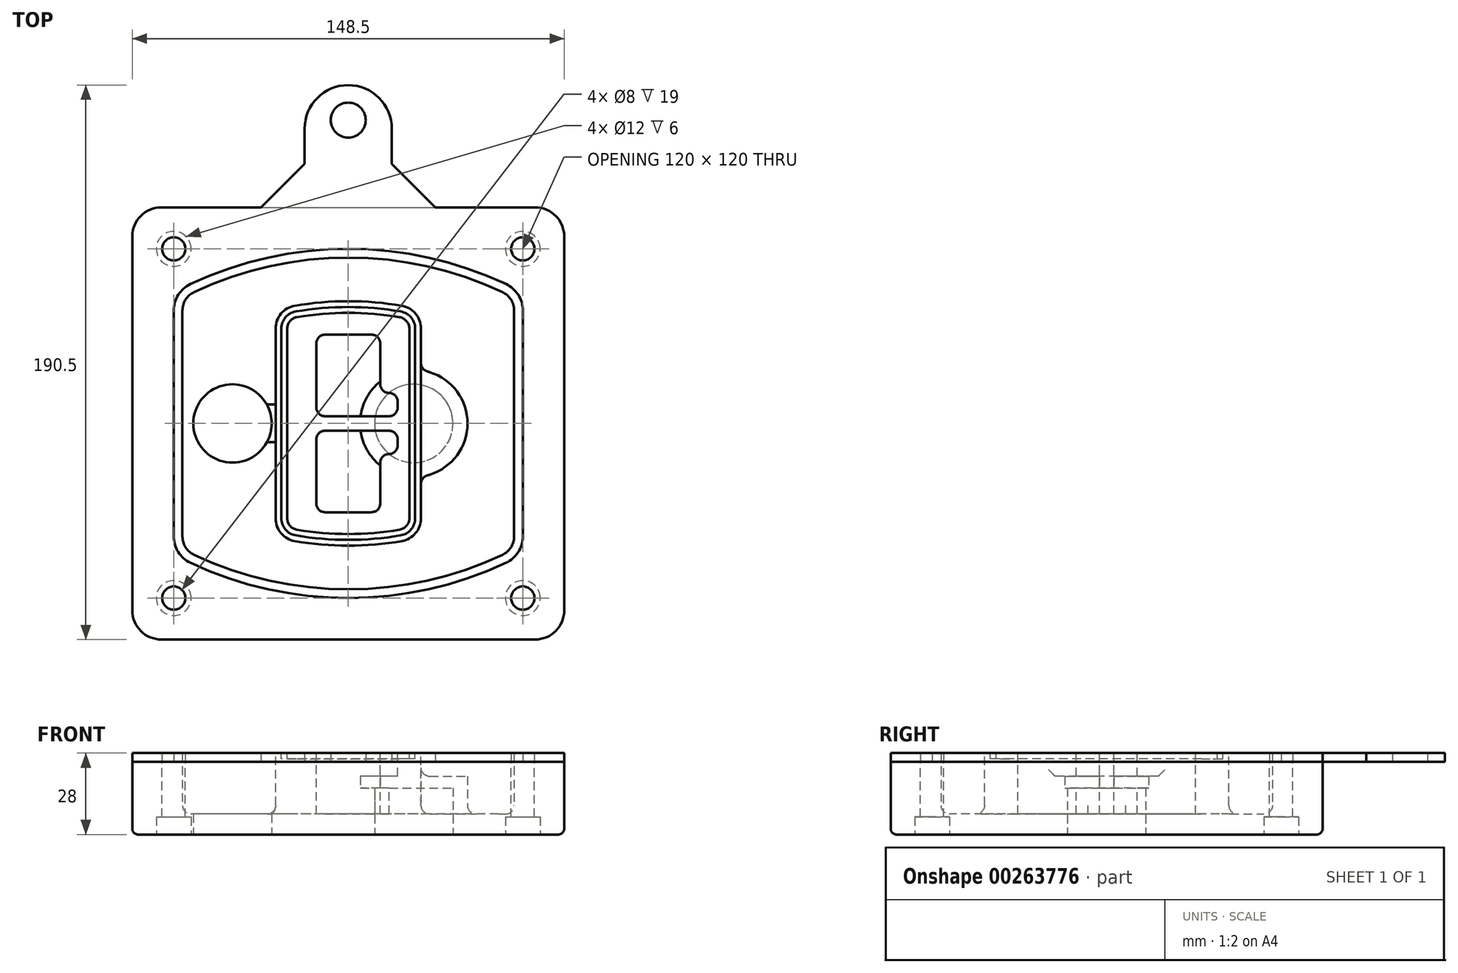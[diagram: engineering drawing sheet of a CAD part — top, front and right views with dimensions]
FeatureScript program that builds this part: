
annotation { "Feature Type Name" : "Feature", "Feature Type Description" : "" }
export const myFeature = defineFeature(function(context is Context, id is Id, definition is map)
    precondition{}
    {
        {
            var Q0;
            Q0=qCreatedBy(makeId("Top.planeOp"),FACE);
            var sketch = newSketch(context, id + "F0", { "sketchPlane" : qUnion([Q0])});
            skPoint(sketch, "E0.rect.middle", {"position": v(0, 0) * mm});
            skLineSegment(sketch, "E1.bottom", {"start": v(-64.25, -74.25) * mm, "end": v(64.25, -74.25) * mm});
            skLineSegment(sketch, "E1.top", {"start": v(-64.25, 74.25) * mm, "end": v(64.25, 74.25) * mm});
            skLineSegment(sketch, "E1.left", {"start": v(-74.25, -64.25) * mm, "end": v(-74.25, 64.25) * mm});
            skLineSegment(sketch, "E1.right", {"start": v(74.25, -64.25) * mm, "end": v(74.25, 64.25) * mm});
            skLineSegment(sketch, "E2", {"start": v(-74.25, 74.25) * mm, "end": v(74.25, -74.25) * mm, "construction": true});
            skLineSegment(sketch, "E3", {"start": v(74.25, 74.25) * mm, "end": v(-74.25, -74.25) * mm, "construction": true});
            skCircle(sketch, "E4", {"center": v(-60, 60) * mm, "radius": 4 * mm});
            skCircle(sketch, "E5", {"center": v(60, 60) * mm, "radius": 4 * mm});
            skCircle(sketch, "E6", {"center": v(60, -60) * mm, "radius": 4 * mm});
            skCircle(sketch, "E7", {"center": v(-60, -60) * mm, "radius": 4 * mm});
            skLineSegment(sketch, "E8", {"start": v(-60, 60) * mm, "end": v(60, 60) * mm, "construction": true});
            skLineSegment(sketch, "E9", {"start": v(60, 60) * mm, "end": v(60, -60) * mm, "construction": true});
            skLineSegment(sketch, "E10", {"start": v(60, -60) * mm, "end": v(-60, -60) * mm, "construction": true});
            skLineSegment(sketch, "E11", {"start": v(-60, -60) * mm, "end": v(-60, 60) * mm, "construction": true});
            skLineSegment(sketch, "E12", {"start": v(-60, 38.83) * mm, "end": v(-60, -38.83) * mm});
            skLineSegment(sketch, "E13", {"start": v(60, 38.83) * mm, "end": v(60, -38.83) * mm});
            skArc(sketch, "E14", {"start": v(54.26, 47.88) * mm, "mid": v(0, 60) * mm, "end": v(-54.26, 47.88) * mm});
            skArc(sketch, "E15", {"start": v(-54.26, -47.88) * mm, "mid": v(0, -60) * mm, "end": v(54.26, -47.88) * mm});
            skLineSegment(sketch, "E16", {"start": v(-60, 0) * mm, "end": v(60, 0) * mm, "construction": true});
            skPoint(sketch, "E17.visualSharp", {"position": v(-60, -45) * mm});
            skArc(sketch, "E17.filletArc", {"start": v(-60, -38.83) * mm, "mid": v(-58.44, -44.2) * mm, "end": v(-54.26, -47.88) * mm});
            skPoint(sketch, "E18.visualSharp", {"position": v(-60, 45) * mm});
            skArc(sketch, "E18.filletArc", {"start": v(-54.26, 47.88) * mm, "mid": v(-58.44, 44.2) * mm, "end": v(-60, 38.83) * mm});
            skPoint(sketch, "E19.visualSharp", {"position": v(60, 45) * mm});
            skArc(sketch, "E19.filletArc", {"start": v(60, 38.83) * mm, "mid": v(58.44, 44.2) * mm, "end": v(54.26, 47.88) * mm});
            skPoint(sketch, "E20.visualSharp", {"position": v(60, -45) * mm});
            skArc(sketch, "E20.filletArc", {"start": v(54.26, -47.88) * mm, "mid": v(58.44, -44.2) * mm, "end": v(60, -38.83) * mm});
            skPoint(sketch, "E21.visualSharp", {"position": v(-74.25, 74.25) * mm});
            skArc(sketch, "E21.filletArc", {"start": v(-64.25, 74.25) * mm, "mid": v(-71.32, 71.32) * mm, "end": v(-74.25, 64.25) * mm});
            skPoint(sketch, "E22.visualSharp", {"position": v(74.25, 74.25) * mm});
            skArc(sketch, "E22.filletArc", {"start": v(74.25, 64.25) * mm, "mid": v(71.32, 71.32) * mm, "end": v(64.25, 74.25) * mm});
            skPoint(sketch, "E23.visualSharp", {"position": v(74.25, -74.25) * mm});
            skArc(sketch, "E23.filletArc", {"start": v(64.25, -74.25) * mm, "mid": v(71.32, -71.32) * mm, "end": v(74.25, -64.25) * mm});
            skPoint(sketch, "E24.visualSharp", {"position": v(-74.25, -74.25) * mm});
            skArc(sketch, "E24.filletArc", {"start": v(-74.25, -64.25) * mm, "mid": v(-71.32, -71.32) * mm, "end": v(-64.25, -74.25) * mm});
            skArc(sketch, "E25.0", {"start": v(57, 38.83) * mm, "mid": v(55.9, 42.58) * mm, "end": v(52.98, 45.17) * mm});
            skLineSegment(sketch, "E25.1", {"start": v(57, 38.83) * mm, "end": v(57, -38.83) * mm});
            skArc(sketch, "E25.2", {"start": v(52.98, -45.17) * mm, "mid": v(55.9, -42.58) * mm, "end": v(57, -38.83) * mm});
            skArc(sketch, "E25.3", {"start": v(-52.98, -45.17) * mm, "mid": v(0, -57) * mm, "end": v(52.98, -45.17) * mm});
            skArc(sketch, "E25.4", {"start": v(-57, -38.83) * mm, "mid": v(-55.9, -42.58) * mm, "end": v(-52.98, -45.17) * mm});
            skArc(sketch, "E25.5", {"start": v(52.98, 45.17) * mm, "mid": v(0, 57) * mm, "end": v(-52.98, 45.17) * mm});
            skLineSegment(sketch, "E25.6", {"start": v(-57, 38.83) * mm, "end": v(-57, -38.83) * mm});
            skArc(sketch, "E25.7", {"start": v(-52.98, 45.17) * mm, "mid": v(-55.9, 42.58) * mm, "end": v(-57, 38.83) * mm});
            skArc(sketch, "E26.0", {"start": v(-55.96, 51.5) * mm, "mid": v(-61.82, 46.33) * mm, "end": v(-64, 38.83) * mm});
            skArc(sketch, "E26.1", {"start": v(55.96, 51.5) * mm, "mid": v(0, 64) * mm, "end": v(-55.96, 51.5) * mm});
            skArc(sketch, "E26.2", {"start": v(64, 38.83) * mm, "mid": v(61.82, 46.33) * mm, "end": v(55.96, 51.5) * mm});
            skLineSegment(sketch, "E26.3", {"start": v(64, 38.83) * mm, "end": v(64, -38.83) * mm});
            skArc(sketch, "E26.4", {"start": v(55.96, -51.5) * mm, "mid": v(61.82, -46.33) * mm, "end": v(64, -38.83) * mm});
            skLineSegment(sketch, "E26.5", {"start": v(-64, 38.83) * mm, "end": v(-64, -38.83) * mm});
            skArc(sketch, "E26.6", {"start": v(-55.96, -51.5) * mm, "mid": v(0, -64) * mm, "end": v(55.96, -51.5) * mm});
            skArc(sketch, "E26.7", {"start": v(-64, -38.83) * mm, "mid": v(-61.82, -46.33) * mm, "end": v(-55.96, -51.5) * mm});
            skSolve(sketch);
        }
        {
            var Q0;
            Q0=makeQuery(id+"F0.imprint","IMPRINT",FACE,{"disambiguationData":[TD([[makeQuery(id+"F0.imprint","IMPRINT",EDGE,{"derivedFrom":sQuery(id+"F0.wireOp",EDGE,"E1.bottom")}),1.0]])]});
            var Q1;
            Q1=makeQuery(id+"F0.imprint","IMPRINT",FACE,{"disambiguationData":[TD([[makeQuery(id+"F0.imprint","IMPRINT",EDGE,{"derivedFrom":sQuery(id+"F0.wireOp",EDGE,"E12")}),1.0]])]});
            var Q2;
            Q2=makeQuery(id+"F0.imprint","IMPRINT",FACE,{"disambiguationData":[TD([[makeQuery(id+"F0.imprint","IMPRINT",EDGE,{"derivedFrom":sQuery(id+"F0.wireOp",EDGE,"E25.0")}),1.0]])]});
            var Q3;
            Q3=makeQuery(id+"F0.imprint","IMPRINT",FACE,{"disambiguationData":[TD([[makeQuery(id+"F0.imprint","IMPRINT",EDGE,{"derivedFrom":sQuery(id+"F0.wireOp",EDGE,"E12")}),-1.0]])]});
            extrude(context, id + "F1", {"entities" : qUnion([Q0, Q1, Q2, Q3]), "oppositeDirection" : true, "depth" : 25 * mm});
        }
        {
            var Q0;
            Q0=makeQuery(id+"F0.imprint","IMPRINT",FACE,{"disambiguationData":[TD([[makeQuery(id+"F0.imprint","IMPRINT",EDGE,{"derivedFrom":sQuery(id+"F0.wireOp",EDGE,"E12")}),1.0]])]});
            extrude(context, id + "F2", {"entities" : qUnion([Q0]), "operationType" : NewBodyOperationType.ADD, "depth" : 3 * mm});
        }
        {
            var Q0;
            Q0=makeQuery(id+"F0.imprint","IMPRINT",FACE,{"disambiguationData":[TD([[makeQuery(id+"F0.imprint","IMPRINT",EDGE,{"derivedFrom":sQuery(id+"F0.wireOp",EDGE,"E25.0")}),1.0]])]});
            extrude(context, id + "F3", {"entities" : qUnion([Q0]), "operationType" : NewBodyOperationType.REMOVE, "oppositeDirection" : true, "depth" : 18 * mm});
        }
        {
            var Q0;
            Q0=makeQuery(id+"F2.opExtrude","CAP_FACE",FACE,{"disambiguationData":[OSD([sQuery(id+"F0.wireOp",EDGE,"E12"),sQuery(id+"F0.wireOp",EDGE,"E13"),sQuery(id+"F0.wireOp",EDGE,"E14"),sQuery(id+"F0.wireOp",EDGE,"E15"),sQuery(id+"F0.wireOp",EDGE,"E17.filletArc"),sQuery(id+"F0.wireOp",EDGE,"E18.filletArc"),sQuery(id+"F0.wireOp",EDGE,"E19.filletArc"),sQuery(id+"F0.wireOp",EDGE,"E20.filletArc"),sQuery(id+"F0.wireOp",EDGE,"E25.0"),sQuery(id+"F0.wireOp",EDGE,"E25.1"),sQuery(id+"F0.wireOp",EDGE,"E25.2"),sQuery(id+"F0.wireOp",EDGE,"E25.3"),sQuery(id+"F0.wireOp",EDGE,"E25.4"),sQuery(id+"F0.wireOp",EDGE,"E25.5"),sQuery(id+"F0.wireOp",EDGE,"E25.6"),sQuery(id+"F0.wireOp",EDGE,"E25.7")])],"isStart":false});
            var sketch = newSketch(context, id + "F4", { "sketchPlane" : qUnion([Q0])});
            skArc(sketch, "E27.0", {"start": v(-18.34, -40.45) * mm, "mid": v(0, -42) * mm, "end": v(18.34, -40.45) * mm});
            skArc(sketch, "E28.0", {"start": v(18.34, 40.45) * mm, "mid": v(0, 42) * mm, "end": v(-18.34, 40.45) * mm});
            skLineSegment(sketch, "E29", {"start": v(-25, 32.57) * mm, "end": v(-25, -32.57) * mm});
            skLineSegment(sketch, "E30", {"start": v(25, 32.57) * mm, "end": v(25, -32.57) * mm});
            skLineSegment(sketch, "E31", {"start": v(-25, 39.1) * mm, "end": v(25, 39.1) * mm, "construction": true});
            skLineSegment(sketch, "E32", {"start": v(-25, -39.1) * mm, "end": v(25, -39.1) * mm, "construction": true});
            skPoint(sketch, "E33.visualSharp", {"position": v(-25, 39.1) * mm});
            skArc(sketch, "E33.filletArc", {"start": v(-18.34, 40.45) * mm, "mid": v(-23.11, 37.73) * mm, "end": v(-25, 32.57) * mm});
            skPoint(sketch, "E34.visualSharp", {"position": v(25, 39.1) * mm});
            skArc(sketch, "E34.filletArc", {"start": v(25, 32.57) * mm, "mid": v(23.11, 37.73) * mm, "end": v(18.34, 40.45) * mm});
            skPoint(sketch, "E35.visualSharp", {"position": v(25, -39.1) * mm});
            skArc(sketch, "E35.filletArc", {"start": v(18.34, -40.45) * mm, "mid": v(23.11, -37.73) * mm, "end": v(25, -32.57) * mm});
            skPoint(sketch, "E36.visualSharp", {"position": v(-25, -39.1) * mm});
            skArc(sketch, "E36.filletArc", {"start": v(-25, -32.57) * mm, "mid": v(-23.11, -37.73) * mm, "end": v(-18.34, -40.45) * mm});
            skArc(sketch, "E37.0", {"start": v(52.98, 45.17) * mm, "mid": v(0, 57) * mm, "end": v(-52.98, 45.17) * mm});
            skArc(sketch, "E37.1", {"start": v(-52.98, 45.17) * mm, "mid": v(-55.9, 42.58) * mm, "end": v(-57, 38.83) * mm});
            skLineSegment(sketch, "E37.2", {"start": v(-57, 38.83) * mm, "end": v(-57, -38.83) * mm});
            skArc(sketch, "E37.3", {"start": v(-57, -38.83) * mm, "mid": v(-55.9, -42.58) * mm, "end": v(-52.98, -45.17) * mm});
            skArc(sketch, "E37.4", {"start": v(-52.98, -45.17) * mm, "mid": v(0, -57) * mm, "end": v(52.98, -45.17) * mm});
            skArc(sketch, "E37.5", {"start": v(52.98, -45.17) * mm, "mid": v(55.9, -42.58) * mm, "end": v(57, -38.83) * mm});
            skLineSegment(sketch, "E37.6", {"start": v(57, 38.83) * mm, "end": v(57, -38.83) * mm});
            skArc(sketch, "E37.7", {"start": v(57, 38.83) * mm, "mid": v(55.9, 42.58) * mm, "end": v(52.98, 45.17) * mm});
            skLineSegment(sketch, "E38.0", {"start": v(23, 32.57) * mm, "end": v(23, -32.57) * mm});
            skArc(sketch, "E38.1", {"start": v(18, -38.48) * mm, "mid": v(21.58, -36.44) * mm, "end": v(23, -32.57) * mm});
            skArc(sketch, "E38.2", {"start": v(-18, -38.48) * mm, "mid": v(0, -40) * mm, "end": v(18, -38.48) * mm});
            skArc(sketch, "E38.3", {"start": v(-23, -32.57) * mm, "mid": v(-21.58, -36.44) * mm, "end": v(-18, -38.48) * mm});
            skLineSegment(sketch, "E38.4", {"start": v(-23, 32.57) * mm, "end": v(-23, -32.57) * mm});
            skArc(sketch, "E38.5", {"start": v(23, 32.57) * mm, "mid": v(21.58, 36.44) * mm, "end": v(18, 38.48) * mm});
            skArc(sketch, "E38.6", {"start": v(-18, 38.48) * mm, "mid": v(-21.58, 36.44) * mm, "end": v(-23, 32.57) * mm});
            skArc(sketch, "E38.7", {"start": v(18, 38.48) * mm, "mid": v(0, 40) * mm, "end": v(-18, 38.48) * mm});
            skArc(sketch, "E39.0", {"start": v(21, 32.57) * mm, "mid": v(20.06, 35.15) * mm, "end": v(17.67, 36.5) * mm});
            skLineSegment(sketch, "E39.1", {"start": v(21, 32.57) * mm, "end": v(21, -32.57) * mm});
            skArc(sketch, "E39.2", {"start": v(17.67, -36.5) * mm, "mid": v(20.06, -35.15) * mm, "end": v(21, -32.57) * mm});
            skArc(sketch, "E39.3", {"start": v(-17.67, -36.5) * mm, "mid": v(0, -38) * mm, "end": v(17.67, -36.5) * mm});
            skArc(sketch, "E39.4", {"start": v(-21, -32.57) * mm, "mid": v(-20.06, -35.15) * mm, "end": v(-17.67, -36.5) * mm});
            skArc(sketch, "E39.5", {"start": v(17.67, 36.5) * mm, "mid": v(0, 38) * mm, "end": v(-17.67, 36.5) * mm});
            skLineSegment(sketch, "E39.6", {"start": v(-21, 32.57) * mm, "end": v(-21, -32.57) * mm});
            skArc(sketch, "E39.7", {"start": v(-17.67, 36.5) * mm, "mid": v(-20.06, 35.15) * mm, "end": v(-21, 32.57) * mm});
            skLineSegment(sketch, "E40", {"start": v(-25, 0) * mm, "end": v(25, 0) * mm, "construction": true});
            skLineSegment(sketch, "E41", {"start": v(-11, 5.5) * mm, "end": v(-11, 27.5) * mm});
            skLineSegment(sketch, "E42", {"start": v(-8, 30.5) * mm, "end": v(8, 30.5) * mm});
            skLineSegment(sketch, "E43", {"start": v(11, 27.5) * mm, "end": v(11, 13.5) * mm});
            skLineSegment(sketch, "E44", {"start": v(14, 10.5) * mm, "end": v(14, 10.5) * mm});
            skLineSegment(sketch, "E45", {"start": v(17, 7.5) * mm, "end": v(17, 5.5) * mm});
            skLineSegment(sketch, "E46", {"start": v(14, 2.5) * mm, "end": v(-8, 2.5) * mm});
            skPoint(sketch, "E47.visualSharp", {"position": v(-11, 30.5) * mm});
            skArc(sketch, "E47.filletArc", {"start": v(-8, 30.5) * mm, "mid": v(-10.12, 29.62) * mm, "end": v(-11, 27.5) * mm});
            skPoint(sketch, "E48.visualSharp", {"position": v(11, 30.5) * mm});
            skArc(sketch, "E48.filletArc", {"start": v(11, 27.5) * mm, "mid": v(10.12, 29.62) * mm, "end": v(8, 30.5) * mm});
            skPoint(sketch, "E49.visualSharp", {"position": v(11, 10.5) * mm});
            skArc(sketch, "E49.filletArc", {"start": v(11, 13.5) * mm, "mid": v(11.88, 11.38) * mm, "end": v(14, 10.5) * mm});
            skPoint(sketch, "E50.visualSharp", {"position": v(17, 10.5) * mm});
            skArc(sketch, "E50.filletArc", {"start": v(17, 7.5) * mm, "mid": v(16.12, 9.62) * mm, "end": v(14, 10.5) * mm});
            skPoint(sketch, "E51.visualSharp", {"position": v(17, 2.5) * mm});
            skArc(sketch, "E51.filletArc", {"start": v(14, 2.5) * mm, "mid": v(16.12, 3.38) * mm, "end": v(17, 5.5) * mm});
            skPoint(sketch, "E52.visualSharp", {"position": v(-11, 2.5) * mm});
            skArc(sketch, "E52.filletArc", {"start": v(-11, 5.5) * mm, "mid": v(-10.12, 3.38) * mm, "end": v(-8, 2.5) * mm});
            skLineSegment(sketch, "E53.0.MirrorCS", {"start": v(14, -2.5) * mm, "end": v(-8, -2.5) * mm});
            skArc(sketch, "E54.0.MirrorCS", {"start": v(-11, -5.5) * mm, "mid": v(-10.12, -3.38) * mm, "end": v(-8, -2.5) * mm});
            skLineSegment(sketch, "E55.0.MirrorCS", {"start": v(-11, -5.5) * mm, "end": v(-11, -27.5) * mm});
            skArc(sketch, "E56.0.MirrorCS", {"start": v(-8, -30.5) * mm, "mid": v(-10.12, -29.62) * mm, "end": v(-11, -27.5) * mm});
            skLineSegment(sketch, "E57.0.MirrorCS", {"start": v(-8, -30.5) * mm, "end": v(8, -30.5) * mm});
            skArc(sketch, "E58.0.MirrorCS", {"start": v(11, -27.5) * mm, "mid": v(10.12, -29.62) * mm, "end": v(8, -30.5) * mm});
            skLineSegment(sketch, "E59.0.MirrorCS", {"start": v(11, -27.5) * mm, "end": v(11, -13.5) * mm});
            skArc(sketch, "E60.0.MirrorCS", {"start": v(11, -13.5) * mm, "mid": v(11.88, -11.38) * mm, "end": v(14, -10.5) * mm});
            skArc(sketch, "E61.0.MirrorCS", {"start": v(17, -7.5) * mm, "mid": v(16.12, -9.62) * mm, "end": v(14, -10.5) * mm});
            skLineSegment(sketch, "E62.0.MirrorCS", {"start": v(17, -7.5) * mm, "end": v(17, -5.5) * mm});
            skArc(sketch, "E63.0.MirrorCS", {"start": v(14, -2.5) * mm, "mid": v(16.12, -3.38) * mm, "end": v(17, -5.5) * mm});
            skSolve(sketch);
        }
        {
            var Q0;
            Q0=makeQuery(id+"F4.imprint","IMPRINT",FACE,{"disambiguationData":[TD([[makeQuery(id+"F4.imprint","IMPRINT",EDGE,{"derivedFrom":sQuery(id+"F4.wireOp",EDGE,"E27.0")}),1.0]])]});
            var Q1;
            Q1=makeQuery(id+"F4.imprint","IMPRINT",FACE,{"disambiguationData":[TD([[makeQuery(id+"F4.imprint","IMPRINT",EDGE,{"derivedFrom":sQuery(id+"F4.wireOp",EDGE,"E38.0")}),-1.0]])]});
            var Q2;
            Q2=makeQuery(id+"F4.imprint","IMPRINT",FACE,{"disambiguationData":[TD([[makeQuery(id+"F4.imprint","IMPRINT",EDGE,{"derivedFrom":sQuery(id+"F4.wireOp",EDGE,"E39.0")}),1.0]])]});
            extrude(context, id + "F5", {"entities" : qUnion([Q0, Q1, Q2]), "operationType" : NewBodyOperationType.ADD, "endBound" : BoundingType.UP_TO_NEXT, "oppositeDirection" : true, "depth" : 25 * mm});
        }
        {
            var Q0;
            Q0=makeQuery(id+"F4.imprint","IMPRINT",FACE,{"disambiguationData":[TD([[makeQuery(id+"F4.imprint","IMPRINT",EDGE,{"derivedFrom":sQuery(id+"F4.wireOp",EDGE,"E38.0")}),-1.0]])]});
            extrude(context, id + "F6", {"entities" : qUnion([Q0]), "operationType" : NewBodyOperationType.REMOVE, "oppositeDirection" : true, "depth" : 2 * mm});
        }
        {
            var Q0;
            Q0=makeQuery(id+"F1.opExtrude","CAP_FACE",FACE,{"disambiguationData":[OSD([sQuery(id+"F0.wireOp",EDGE,"E1.bottom"),sQuery(id+"F0.wireOp",EDGE,"E1.top"),sQuery(id+"F0.wireOp",EDGE,"E1.left"),sQuery(id+"F0.wireOp",EDGE,"E1.right"),sQuery(id+"F0.wireOp",EDGE,"E4"),sQuery(id+"F0.wireOp",EDGE,"E5"),sQuery(id+"F0.wireOp",EDGE,"E6"),sQuery(id+"F0.wireOp",EDGE,"E7"),sQuery(id+"F0.wireOp",EDGE,"E21.filletArc"),sQuery(id+"F0.wireOp",EDGE,"E22.filletArc"),sQuery(id+"F0.wireOp",EDGE,"E23.filletArc"),sQuery(id+"F0.wireOp",EDGE,"E24.filletArc")])],"isStart":false});
            var sketch = newSketch(context, id + "F7", { "sketchPlane" : qUnion([Q0])});
            skCircle(sketch, "E64", {"center": v(22.5, 0) * mm, "radius": 13.47 * mm});
            skCircle(sketch, "E65", {"center": v(-39.81, 0) * mm, "radius": 13.47 * mm});
            skLineSegment(sketch, "E66", {"start": v(74.25, 0) * mm, "end": v(-74.25, 0) * mm});
            skCircle(sketch, "E67", {"center": v(22.5, 0) * mm, "radius": 18.47 * mm});
            skCircle(sketch, "E68", {"center": v(60, -60) * mm, "radius": 6 * mm});
            skCircle(sketch, "E69", {"center": v(-60, -60) * mm, "radius": 6 * mm});
            skCircle(sketch, "E70", {"center": v(-60, 60) * mm, "radius": 6 * mm});
            skCircle(sketch, "E71", {"center": v(60, 60) * mm, "radius": 6 * mm});
            skSolve(sketch);
        }
        {
            var Q0;
            {var subQ1=sQuery(id+"F7.wireOp",EDGE,"E66");var subQ4=sQuery(id+"F7.wireOp",EDGE,"E64");var subQ6=makeQuery(id+"F7.imprint","INTERSECT",VERTEX,{"disambiguationData":[OD(0.0)],"derivedFrom":[subQ4,subQ1]});Q0=makeQuery(id+"F7.imprint","IMPRINT",FACE,{"disambiguationData":[TD([[makeQuery(id+"F7.imprint","IMPRINT",EDGE,{"disambiguationData":[TD([[subQ6,-1.0]])],"derivedFrom":subQ4}),-1.0]])]});}
            var Q1;
            {var subQ0=sQuery(id+"F7.wireOp",EDGE,"E66");var subQ1=sQuery(id+"F7.wireOp",EDGE,"E64");var subQ3=makeQuery(id+"F7.imprint","INTERSECT",VERTEX,{"disambiguationData":[OD(0.0)],"derivedFrom":[subQ1,subQ0]});Q1=makeQuery(id+"F7.imprint","IMPRINT",FACE,{"disambiguationData":[TD([[makeQuery(id+"F7.imprint","IMPRINT",EDGE,{"disambiguationData":[TD([[subQ3,-1.0]])],"derivedFrom":subQ1}),1.0]])]});}
            var Q2;
            {var subQ0=sQuery(id+"F7.wireOp",EDGE,"E66");var subQ1=sQuery(id+"F7.wireOp",EDGE,"E64");var subQ3=makeQuery(id+"F7.imprint","INTERSECT",VERTEX,{"disambiguationData":[OD(0.0)],"derivedFrom":[subQ1,subQ0]});Q2=makeQuery(id+"F7.imprint","IMPRINT",FACE,{"disambiguationData":[TD([[makeQuery(id+"F7.imprint","IMPRINT",EDGE,{"disambiguationData":[TD([[subQ3,1.0]])],"derivedFrom":subQ1}),1.0]])]});}
            var Q3;
            {var subQ1=sQuery(id+"F7.wireOp",EDGE,"E66");var subQ4=sQuery(id+"F7.wireOp",EDGE,"E64");var subQ6=makeQuery(id+"F7.imprint","INTERSECT",VERTEX,{"disambiguationData":[OD(0.0)],"derivedFrom":[subQ4,subQ1]});Q3=makeQuery(id+"F7.imprint","IMPRINT",FACE,{"disambiguationData":[TD([[makeQuery(id+"F7.imprint","IMPRINT",EDGE,{"disambiguationData":[TD([[subQ6,1.0]])],"derivedFrom":subQ4}),-1.0]])]});}
            extrude(context, id + "F8", {"entities" : qUnion([Q0, Q1, Q2, Q3]), "operationType" : NewBodyOperationType.ADD, "oppositeDirection" : true, "depth" : 20 * mm});
        }
        {
            var Q0;
            {var subQ0=sQuery(id+"F7.wireOp",EDGE,"E66");var subQ1=sQuery(id+"F7.wireOp",EDGE,"E64");var subQ3=makeQuery(id+"F7.imprint","INTERSECT",VERTEX,{"disambiguationData":[OD(0.0)],"derivedFrom":[subQ1,subQ0]});Q0=makeQuery(id+"F7.imprint","IMPRINT",FACE,{"disambiguationData":[TD([[makeQuery(id+"F7.imprint","IMPRINT",EDGE,{"disambiguationData":[TD([[subQ3,-1.0]])],"derivedFrom":subQ1}),1.0]])]});}
            var Q1;
            {var subQ0=sQuery(id+"F7.wireOp",EDGE,"E66");var subQ1=sQuery(id+"F7.wireOp",EDGE,"E64");var subQ3=makeQuery(id+"F7.imprint","INTERSECT",VERTEX,{"disambiguationData":[OD(0.0)],"derivedFrom":[subQ1,subQ0]});Q1=makeQuery(id+"F7.imprint","IMPRINT",FACE,{"disambiguationData":[TD([[makeQuery(id+"F7.imprint","IMPRINT",EDGE,{"disambiguationData":[TD([[subQ3,1.0]])],"derivedFrom":subQ1}),1.0]])]});}
            extrude(context, id + "F9", {"entities" : qUnion([Q0, Q1]), "operationType" : NewBodyOperationType.REMOVE, "oppositeDirection" : true, "depth" : 16 * mm});
        }
        {
            var Q0;
            {var subQ0=sQuery(id+"F7.wireOp",EDGE,"E66");var subQ1=sQuery(id+"F7.wireOp",EDGE,"E65");var subQ3=makeQuery(id+"F7.imprint","INTERSECT",VERTEX,{"disambiguationData":[OD(0.0)],"derivedFrom":[subQ1,subQ0]});Q0=makeQuery(id+"F7.imprint","IMPRINT",FACE,{"disambiguationData":[TD([[makeQuery(id+"F7.imprint","IMPRINT",EDGE,{"disambiguationData":[TD([[subQ3,-1.0]])],"derivedFrom":subQ1}),1.0]])]});}
            var Q1;
            {var subQ0=sQuery(id+"F7.wireOp",EDGE,"E66");var subQ1=sQuery(id+"F7.wireOp",EDGE,"E65");var subQ3=makeQuery(id+"F7.imprint","INTERSECT",VERTEX,{"disambiguationData":[OD(0.0)],"derivedFrom":[subQ1,subQ0]});Q1=makeQuery(id+"F7.imprint","IMPRINT",FACE,{"disambiguationData":[TD([[makeQuery(id+"F7.imprint","IMPRINT",EDGE,{"disambiguationData":[TD([[subQ3,1.0]])],"derivedFrom":subQ1}),1.0]])]});}
            extrude(context, id + "F10", {"entities" : qUnion([Q0, Q1]), "operationType" : NewBodyOperationType.REMOVE, "oppositeDirection" : true, "depth" : 25 * mm});
        }
        {
            var Q0;
            Q0=makeQuery(id+"F7.imprint","IMPRINT",FACE,{"disambiguationData":[TD([[makeQuery(id+"F7.imprint","IMPRINT",EDGE,{"derivedFrom":sQuery(id+"F7.wireOp",EDGE,"E68")}),1.0]])]});
            var Q1;
            Q1=makeQuery(id+"F7.imprint","IMPRINT",FACE,{"disambiguationData":[TD([[makeQuery(id+"F7.imprint","IMPRINT",EDGE,{"derivedFrom":makeQuery(id+"F1.opExtrude","CAP_EDGE",EDGE,{"disambiguationData":[OSD([sQuery(id+"F0.wireOp",EDGE,"E5")])],"isStart":false})}),-1.0]])]});
            var Q2;
            Q2=makeQuery(id+"F7.imprint","IMPRINT",FACE,{"disambiguationData":[TD([[makeQuery(id+"F7.imprint","IMPRINT",EDGE,{"derivedFrom":sQuery(id+"F7.wireOp",EDGE,"E69")}),1.0]])]});
            var Q3;
            Q3=makeQuery(id+"F7.imprint","IMPRINT",FACE,{"disambiguationData":[TD([[makeQuery(id+"F7.imprint","IMPRINT",EDGE,{"derivedFrom":makeQuery(id+"F1.opExtrude","CAP_EDGE",EDGE,{"disambiguationData":[OSD([sQuery(id+"F0.wireOp",EDGE,"E4")])],"isStart":false})}),-1.0]])]});
            var Q4;
            Q4=makeQuery(id+"F7.imprint","IMPRINT",FACE,{"disambiguationData":[TD([[makeQuery(id+"F7.imprint","IMPRINT",EDGE,{"derivedFrom":sQuery(id+"F7.wireOp",EDGE,"E70")}),1.0]])]});
            var Q5;
            Q5=makeQuery(id+"F7.imprint","IMPRINT",FACE,{"disambiguationData":[TD([[makeQuery(id+"F7.imprint","IMPRINT",EDGE,{"derivedFrom":makeQuery(id+"F1.opExtrude","CAP_EDGE",EDGE,{"disambiguationData":[OSD([sQuery(id+"F0.wireOp",EDGE,"E7")])],"isStart":false})}),-1.0]])]});
            var Q6;
            Q6=makeQuery(id+"F7.imprint","IMPRINT",FACE,{"disambiguationData":[TD([[makeQuery(id+"F7.imprint","IMPRINT",EDGE,{"derivedFrom":sQuery(id+"F7.wireOp",EDGE,"E71")}),1.0]])]});
            var Q7;
            Q7=makeQuery(id+"F7.imprint","IMPRINT",FACE,{"disambiguationData":[TD([[makeQuery(id+"F7.imprint","IMPRINT",EDGE,{"derivedFrom":makeQuery(id+"F1.opExtrude","CAP_EDGE",EDGE,{"disambiguationData":[OSD([sQuery(id+"F0.wireOp",EDGE,"E6")])],"isStart":false})}),-1.0]])]});
            extrude(context, id + "F11", {"entities" : qUnion([Q0, Q1, Q2, Q3, Q4, Q5, Q6, Q7]), "operationType" : NewBodyOperationType.REMOVE, "oppositeDirection" : true, "depth" : 6 * mm});
        }
        {
            var Q0;
            Q0=makeQuery(id+"F9.boolean.opBoolean","COPY",FACE,{"derivedFrom":makeQuery(id+"F9.opExtrude","CAP_FACE",FACE,{"disambiguationData":[OSD([sQuery(id+"F7.wireOp",EDGE,"E64")])],"isStart":false})});
            var sketch = newSketch(context, id + "F12", { "sketchPlane" : qUnion([Q0])});
            skArc(sketch, "E72.0", {"start": v(11, 14.45) * mm, "mid": v(6.45, 9.13) * mm, "end": v(4.2, 2.5) * mm});
            skArc(sketch, "E72.1", {"start": v(4.2, -2.5) * mm, "mid": v(6.45, -9.13) * mm, "end": v(11, -14.45) * mm});
            skLineSegment(sketch, "E73", {"start": v(4.2, -2.5) * mm, "end": v(14, -2.5) * mm});
            skLineSegment(sketch, "E74.0", {"start": v(14, 2.5) * mm, "end": v(4.2, 2.5) * mm});
            skArc(sketch, "E74.1", {"start": v(14, 2.5) * mm, "mid": v(16.12, 3.38) * mm, "end": v(17, 5.5) * mm});
            skLineSegment(sketch, "E74.2", {"start": v(17, 7.5) * mm, "end": v(17, 5.5) * mm});
            skArc(sketch, "E74.3", {"start": v(17, 7.5) * mm, "mid": v(16.12, 9.62) * mm, "end": v(14, 10.5) * mm});
            skArc(sketch, "E74.4", {"start": v(11, 13.5) * mm, "mid": v(11.88, 11.38) * mm, "end": v(14, 10.5) * mm});
            skLineSegment(sketch, "E74.5", {"start": v(11, 14.45) * mm, "end": v(11, 13.5) * mm});
            skLineSegment(sketch, "E74.7", {"start": v(14, -2.5) * mm, "end": v(4.2, -2.5) * mm});
            skArc(sketch, "E74.8", {"start": v(14, -2.5) * mm, "mid": v(16.12, -3.38) * mm, "end": v(17, -5.5) * mm});
            skLineSegment(sketch, "E74.9", {"start": v(17, -7.5) * mm, "end": v(17, -5.5) * mm});
            skArc(sketch, "E74.10", {"start": v(17, -7.5) * mm, "mid": v(16.12, -9.62) * mm, "end": v(14, -10.5) * mm});
            skArc(sketch, "E74.11", {"start": v(11, -13.5) * mm, "mid": v(11.88, -11.38) * mm, "end": v(14, -10.5) * mm});
            skLineSegment(sketch, "E74.12", {"start": v(11, -14.45) * mm, "end": v(11, -13.5) * mm});
            skPoint(sketch, "E75.orphan", {"position": v(11, -27.5) * mm});
            skPoint(sketch, "E76.orphan", {"position": v(-8, -2.5) * mm});
            skPoint(sketch, "E77.orphan", {"position": v(-8, 2.5) * mm});
            skPoint(sketch, "E78.orphan", {"position": v(11, 27.5) * mm});
            skSolve(sketch);
        }
        {
            var Q0;
            {var subQ7=sQuery(id+"F12.wireOp",EDGE,"E72.0");var subQ14=sQuery(id+"F12.wireOp",EDGE,"E72.1");var subQ16=sQuery(id+"F12.wireOp",EDGE,"E74.1");var subQ18=sQuery(id+"F12.wireOp",EDGE,"E74.8");Q0=qUnion([makeQuery(id+"F12.imprint","IMPRINT",FACE,{"disambiguationData":[TD([[makeQuery(id+"F12.imprint","IMPRINT",EDGE,{"derivedFrom":subQ7}),1.0]])]}),makeQuery(id+"F12.imprint","IMPRINT",FACE,{"disambiguationData":[TD([[makeQuery(id+"F12.imprint","IMPRINT",EDGE,{"derivedFrom":subQ14}),1.0]])]}),makeQuery(id+"F12.imprint","IMPRINT",FACE,{"disambiguationData":[TD([[makeQuery(id+"F12.imprint","IMPRINT",EDGE,{"derivedFrom":subQ16}),1.0]])]}),makeQuery(id+"F12.imprint","IMPRINT",FACE,{"disambiguationData":[TD([[makeQuery(id+"F12.imprint","IMPRINT",EDGE,{"derivedFrom":subQ18}),-1.0]])]})]);}
            var Q1;
            Q1=makeQuery(id+"F5.boolean.opBoolean","SPLIT",FACE,{"disambiguationData":[TD([makeQuery(id+"F5.opExtrude","SWEPT_FACE",FACE,{"disambiguationData":[OSD([sQuery(id+"F4.wireOp",EDGE,"E41")])]})])],"derivedFrom":makeQuery(id+"F3.boolean.opBoolean","COPY",FACE,{"derivedFrom":makeQuery(id+"F3.opExtrude","CAP_FACE",FACE,{"disambiguationData":[OSD([sQuery(id+"F0.wireOp",EDGE,"E25.0"),sQuery(id+"F0.wireOp",EDGE,"E25.1"),sQuery(id+"F0.wireOp",EDGE,"E25.2"),sQuery(id+"F0.wireOp",EDGE,"E25.3"),sQuery(id+"F0.wireOp",EDGE,"E25.4"),sQuery(id+"F0.wireOp",EDGE,"E25.5"),sQuery(id+"F0.wireOp",EDGE,"E25.6"),sQuery(id+"F0.wireOp",EDGE,"E25.7")])],"isStart":false})})});
            extrude(context, id + "F13", {"entities" : qUnion([Q0]), "operationType" : NewBodyOperationType.REMOVE, "endBound" : BoundingType.UP_TO_SURFACE, "endBoundEntityFace" : qUnion([Q1]), "depth" : 25 * mm});
        }
        {
            var Q0;
            Q0=makeQuery(id+"F3.boolean.opBoolean","COPY",EDGE,{"derivedFrom":makeQuery(id+"F3.opExtrude","CAP_EDGE",EDGE,{"disambiguationData":[OSD([sQuery(id+"F0.wireOp",EDGE,"E25.6")])],"isStart":false})});
            var Q1;
            Q1=makeQuery(id+"F8.boolean.opBoolean","INTERSECT",EDGE,{"derivedFrom":[makeQuery(id+"F5.opExtrude","SWEPT_FACE",FACE,{"disambiguationData":[OSD([sQuery(id+"F4.wireOp",EDGE,"E30")])]}),makeQuery(id+"F8.opExtrude","CAP_FACE",FACE,{"disambiguationData":[OSD([sQuery(id+"F7.wireOp",EDGE,"E67")])],"isStart":false})]});
            var Q2;
            Q2=makeQuery(id+"F8.boolean.opBoolean","INTERSECT",EDGE,{"disambiguationData":[OD(1.0)],"derivedFrom":[makeQuery(id+"F5.opExtrude","SWEPT_FACE",FACE,{"disambiguationData":[OSD([sQuery(id+"F4.wireOp",EDGE,"E30")])]}),makeQuery(id+"F8.opExtrude","SWEPT_FACE",FACE,{"disambiguationData":[OSD([sQuery(id+"F7.wireOp",EDGE,"E67")])]})]});
            var Q3;
            {var subQ0=sQuery(id+"F4.wireOp",EDGE,"E30");Q3=makeQuery(id+"F8.boolean.opBoolean","SPLIT",EDGE,{"disambiguationData":[TD([makeQuery(id+"F5.opExtrude","SWEPT_FACE",FACE,{"disambiguationData":[OSD([sQuery(id+"F4.wireOp",EDGE,"E35.filletArc")])]})])],"derivedFrom":makeQuery(id+"F5.opExtrude","CAP_EDGE",EDGE,{"disambiguationData":[OSD([subQ0])],"isStart":false})});}
            var Q4;
            {var subQ0=sQuery(id+"F0.wireOp",EDGE,"E25.7");var subQ1=sQuery(id+"F0.wireOp",EDGE,"E25.1");var subQ2=sQuery(id+"F0.wireOp",EDGE,"E25.6");var subQ3=sQuery(id+"F0.wireOp",EDGE,"E25.5");var subQ4=sQuery(id+"F0.wireOp",EDGE,"E25.4");var subQ5=sQuery(id+"F0.wireOp",EDGE,"E25.0");var subQ6=sQuery(id+"F0.wireOp",EDGE,"E25.2");var subQ7=sQuery(id+"F0.wireOp",EDGE,"E25.3");Q4=makeQuery(id+"F8.boolean.opBoolean","INTERSECT",EDGE,{"derivedFrom":[makeQuery(id+"F5.boolean.opBoolean","SPLIT",FACE,{"disambiguationData":[TD([makeQuery(id+"F2.opExtrude","SWEPT_FACE",FACE,{"disambiguationData":[OSD([subQ5])]})])],"derivedFrom":makeQuery(id+"F3.boolean.opBoolean","COPY",FACE,{"derivedFrom":makeQuery(id+"F3.opExtrude","CAP_FACE",FACE,{"disambiguationData":[OSD([subQ5,subQ1,subQ6,subQ7,subQ4,subQ3,subQ2,subQ0])],"isStart":false})})}),makeQuery(id+"F8.opExtrude","SWEPT_FACE",FACE,{"disambiguationData":[OSD([sQuery(id+"F7.wireOp",EDGE,"E67")])]})]});}
            var Q5;
            Q5=makeQuery(id+"F8.boolean.opBoolean","INTERSECT",EDGE,{"disambiguationData":[OD(0.0)],"derivedFrom":[makeQuery(id+"F5.opExtrude","SWEPT_FACE",FACE,{"disambiguationData":[OSD([sQuery(id+"F4.wireOp",EDGE,"E30")])]}),makeQuery(id+"F8.opExtrude","SWEPT_FACE",FACE,{"disambiguationData":[OSD([sQuery(id+"F7.wireOp",EDGE,"E67")])]})]});
            fillet(context, id + "F14", {"entities" : qUnion([Q0, Q1, Q2, Q3, Q4, Q5]), "radius" : 3 * mm, "tangentPropagation" : true, "allowEdgeOverflow" : false});
        }
        {
            var Q0;
            Q0=makeQuery(id+"F1.opExtrude","CAP_EDGE",EDGE,{"disambiguationData":[OSD([sQuery(id+"F0.wireOp",EDGE,"E1.bottom")])],"isStart":false});
            fillet(context, id + "F15", {"entities" : qUnion([Q0]), "radius" : 2 * mm, "tangentPropagation" : true, "allowEdgeOverflow" : false});
        }
        {
            var Q0;
            {var subQ0=sQuery(id+"F0.wireOp",EDGE,"E22.filletArc");var subQ1=sQuery(id+"F0.wireOp",EDGE,"E7");var subQ2=sQuery(id+"F0.wireOp",EDGE,"E6");var subQ3=sQuery(id+"F0.wireOp",EDGE,"E5");var subQ4=sQuery(id+"F0.wireOp",EDGE,"E4");var subQ5=sQuery(id+"F0.wireOp",EDGE,"E1.bottom");var subQ6=sQuery(id+"F0.wireOp",EDGE,"E21.filletArc");var subQ7=sQuery(id+"F0.wireOp",EDGE,"E1.top");var subQ8=sQuery(id+"F0.wireOp",EDGE,"E1.left");var subQ9=sQuery(id+"F0.wireOp",EDGE,"E1.right");var subQ10=sQuery(id+"F0.wireOp",EDGE,"E23.filletArc");var subQ11=sQuery(id+"F0.wireOp",EDGE,"E24.filletArc");Q0=makeQuery(id+"F2.boolean.opBoolean","SPLIT",FACE,{"disambiguationData":[TD([makeQuery(id+"F1.opExtrude","SWEPT_FACE",FACE,{"disambiguationData":[OSD([subQ5])]})])],"derivedFrom":makeQuery(id+"F1.opExtrude","CAP_FACE",FACE,{"disambiguationData":[OSD([subQ5,subQ7,subQ8,subQ9,subQ4,subQ3,subQ2,subQ1,subQ6,subQ0,subQ10,subQ11])],"isStart":true})});}
            var sketch = newSketch(context, id + "F16", { "sketchPlane" : qUnion([Q0])});
            skLineSegment(sketch, "E79", {"start": v(0, 74.25) * mm, "end": v(0, 104.25) * mm, "construction": true});
            skCircle(sketch, "E80", {"center": v(0, 104.25) * mm, "radius": 6 * mm});
            skLineSegment(sketch, "E81", {"start": v(-30.01, 74.25) * mm, "end": v(-15.01, 89.25) * mm});
            skPoint(sketch, "E81.endSnap0", {"position": v(0, 89.25) * mm});
            skLineSegment(sketch, "E82", {"start": v(29.99, 74.25) * mm, "end": v(14.99, 89.25) * mm});
            skLineSegment(sketch, "E83", {"start": v(-15.01, 89.25) * mm, "end": v(-15.01, 101.25) * mm});
            skLineSegment(sketch, "E84", {"start": v(14.99, 89.25) * mm, "end": v(14.99, 101.25) * mm});
            skArc(sketch, "E85", {"start": v(14.99, 101.25) * mm, "mid": v(-0.01, 116.25) * mm, "end": v(-15.01, 101.25) * mm});
            skLineSegment(sketch, "E86", {"start": v(-102.32, 0) * mm, "end": v(99.78, 0) * mm, "construction": true});
            skArc(sketch, "E87.MirrorCS", {"start": v(14.99, -101.25) * mm, "mid": v(-0.01, -116.25) * mm, "end": v(-15.01, -101.25) * mm});
            skLineSegment(sketch, "E88.MirrorCS", {"start": v(-15.01, -89.25) * mm, "end": v(-15.01, -101.25) * mm});
            skLineSegment(sketch, "E89.MirrorCS", {"start": v(14.99, -89.25) * mm, "end": v(14.99, -101.25) * mm});
            skLineSegment(sketch, "E90.MirrorCS", {"start": v(29.99, -74.25) * mm, "end": v(14.99, -89.25) * mm});
            skPoint(sketch, "E91.MirrorP", {"position": v(0, -89.25) * mm});
            skLineSegment(sketch, "E92.MirrorCS", {"start": v(0, -74.25) * mm, "end": v(0, -104.25) * mm, "construction": true});
            skCircle(sketch, "E93.MirrorC", {"center": v(0, -104.25) * mm, "radius": 6 * mm});
            skLineSegment(sketch, "E94.MirrorCS", {"start": v(-30.01, -74.25) * mm, "end": v(-15.01, -89.25) * mm});
            skSolve(sketch);
        }
        {
            var Q0;
            Q0=makeQuery(id+"F16.imprint","IMPRINT",FACE,{"disambiguationData":[TD([[makeQuery(id+"F16.imprint","IMPRINT",EDGE,{"derivedFrom":sQuery(id+"F16.wireOp",EDGE,"E87.MirrorCS")}),-1.0]])]});
            var Q1;
            Q1=makeQuery(id+"F16.imprint","IMPRINT",FACE,{"disambiguationData":[TD([[makeQuery(id+"F16.imprint","IMPRINT",EDGE,{"derivedFrom":makeQuery(id+"F1.opExtrude","CAP_EDGE",EDGE,{"disambiguationData":[OSD([sQuery(id+"F0.wireOp",EDGE,"E1.left")])],"isStart":true})}),-1.0]])]});
            var Q2;
            Q2=makeQuery(id+"F16.imprint","IMPRINT",FACE,{"disambiguationData":[TD([[makeQuery(id+"F16.imprint","IMPRINT",EDGE,{"derivedFrom":sQuery(id+"F16.wireOp",EDGE,"E80")}),-1.0]])]});
            extrude(context, id + "F17", {"entities" : qUnion([Q0, Q1, Q2]), "depth" : 3 * mm});
        }
    });
